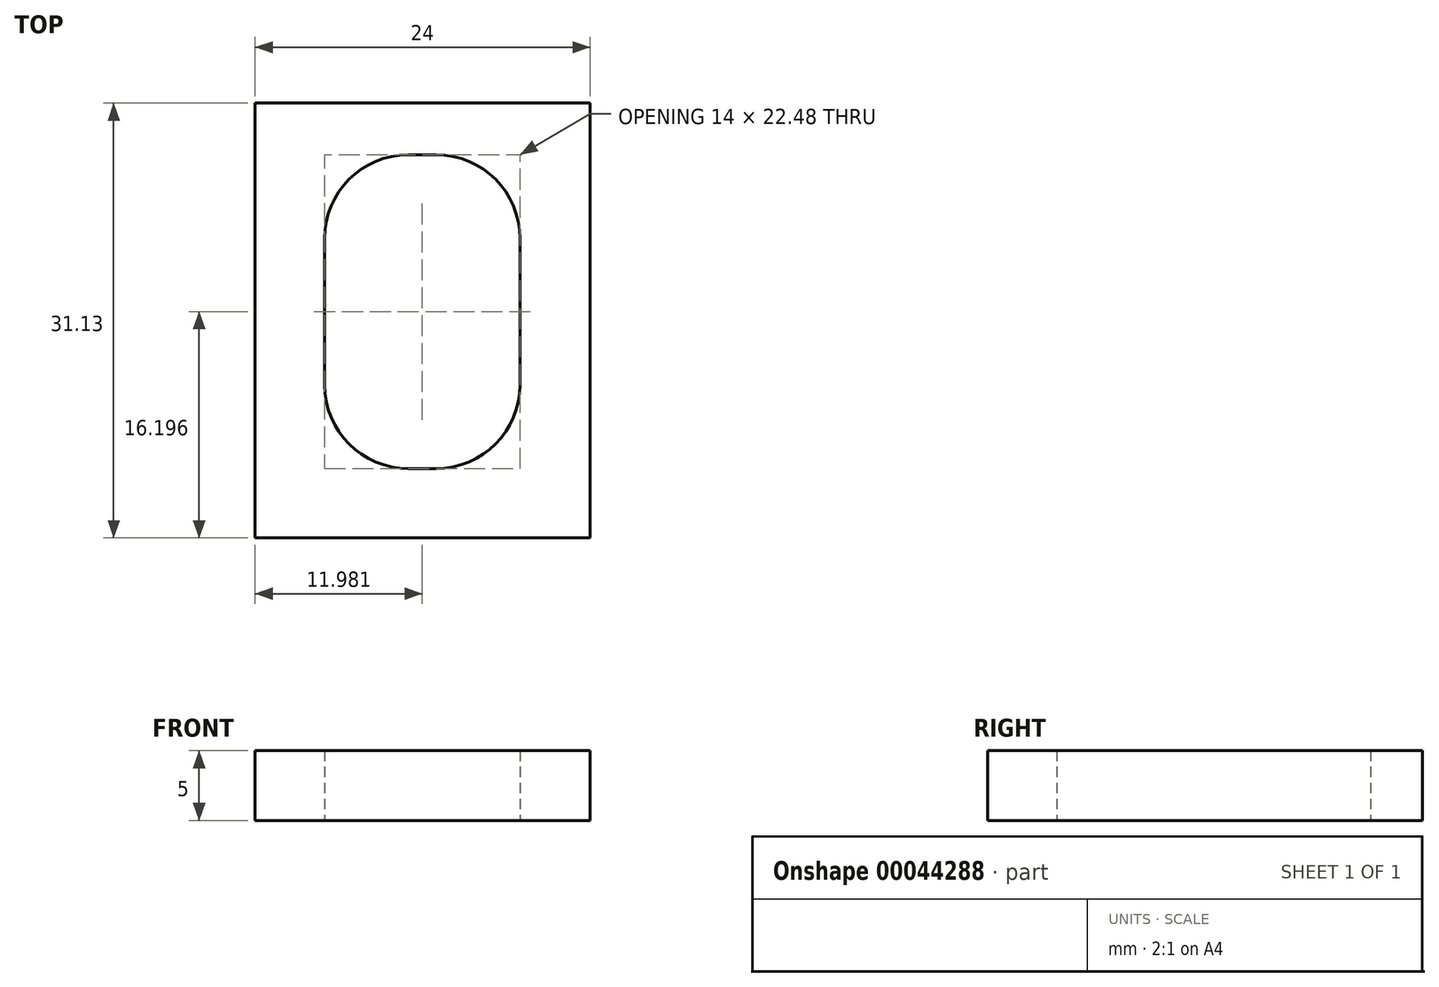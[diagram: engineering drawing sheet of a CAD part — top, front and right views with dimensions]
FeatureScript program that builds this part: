
annotation { "Feature Type Name" : "Feature", "Feature Type Description" : "" }
export const myFeature = defineFeature(function(context is Context, id is Id, definition is map)
    precondition{}
    {
        {
            var Q0;
            Q0=qCreatedBy(makeId("Top.planeOp"),FACE);
            var sketch = newSketch(context, id + "F0", { "sketchPlane" : qUnion([Q0])});
            skLineSegment(sketch, "E0.bottom", {"start": v(0, 0) * mm, "end": v(24, 0) * mm});
            skLineSegment(sketch, "E0.top", {"start": v(0, 31.13) * mm, "end": v(24, 31.13) * mm});
            skLineSegment(sketch, "E0.left", {"start": v(0, 0) * mm, "end": v(0, 31.13) * mm});
            skLineSegment(sketch, "E0.right", {"start": v(24, 0) * mm, "end": v(24, 31.13) * mm});
            skLineSegment(sketch, "E1.bottom", {"start": v(4.98, 4.96) * mm, "end": v(18.98, 4.96) * mm});
            skLineSegment(sketch, "E1.top", {"start": v(4.98, 27.43) * mm, "end": v(18.98, 27.43) * mm});
            skLineSegment(sketch, "E1.left", {"start": v(4.98, 4.96) * mm, "end": v(4.98, 27.43) * mm});
            skLineSegment(sketch, "E1.right", {"start": v(18.98, 4.96) * mm, "end": v(18.98, 27.43) * mm});
            skLineSegment(sketch, "E2", {"start": v(0, 0) * mm, "end": v(4.98, 0) * mm});
            skLineSegment(sketch, "E3", {"start": v(4.98, 0) * mm, "end": v(4.98, 4.96) * mm});
            skSolve(sketch);
        }
        {
            var Q0;
            Q0 = qSketchRegion(id + "F0", true);
            extrude(context, id + "F1", {"entities" : qUnion([Q0]), "depth" : 5 * mm});
        }
        {
            var Q0;
            Q0=makeQuery(id+"F1.opExtrude","SWEPT_EDGE",EDGE,{"disambiguationData":[OSD([sQuery(id+"F0.wireOp",EDGE,"E1.top"),sQuery(id+"F0.wireOp",EDGE,"E1.left")])]});
            var Q1;
            Q1=makeQuery(id+"F1.opExtrude","SWEPT_EDGE",EDGE,{"disambiguationData":[OSD([sQuery(id+"F0.wireOp",EDGE,"E1.bottom"),sQuery(id+"F0.wireOp",EDGE,"E1.left")])]});
            var Q2;
            Q2=makeQuery(id+"F1.opExtrude","SWEPT_EDGE",EDGE,{"disambiguationData":[OSD([sQuery(id+"F0.wireOp",EDGE,"E1.bottom"),sQuery(id+"F0.wireOp",EDGE,"E1.right")])]});
            var Q3;
            Q3=makeQuery(id+"F1.opExtrude","SWEPT_EDGE",EDGE,{"disambiguationData":[OSD([sQuery(id+"F0.wireOp",EDGE,"E1.top"),sQuery(id+"F0.wireOp",EDGE,"E1.right")])]});
            fillet(context, id + "F2", {"entities" : qUnion([Q0, Q1, Q2, Q3]), "radius" : 6 * mm, "tangentPropagation" : true, "allowEdgeOverflow" : false});
        }
    });
